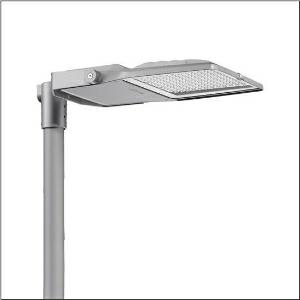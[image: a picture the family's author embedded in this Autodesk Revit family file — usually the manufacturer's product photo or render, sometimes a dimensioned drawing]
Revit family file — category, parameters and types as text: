
# Revit family: floodlight_fl_21_midi___pl33t_5xa7786e2f3a_2de9
name_source: partatom
category: Lighting Fixtures
units: mm (PartAtom-declared; Revit-internal decimal feet)

## family parameters
Cut with Voids When Loaded = No
Host = Face
Light Source = No
Part Type = Normal
Room Calculation Point = No
Round Connector Dimension = Use Diameter
Shared = No

## types (1)
- --- (1 x LED, 26630 lm, 212.4 W, 3000K)
    Apparent Load = 212 VA
    CIE Flux Codes = 26 75 99 100 100
    Color Rendering = 70
    Color Temperature = 3000K
    Default Elevation = 1800 mm
    Description = Floodlight FL 21 midi, floodlight, primary light control with lens, of PMMA, primary optical cover: protective disc, of toughened safety glass, transparent, light distribution: PL33T, light emission: direct distribution, installation type: surface-mounted, LED, High Power LED, rated luminous flux: 26.630lm, luminous efficacy: 125lm/W, light colour: 730, colour temperature: 3000K, control gear: Smart Interface (Zhaga), control: flexible luminous flux parameterisation, time-dependent luminous flux control, constant luminous flux control, overheat protection, pre-setting: logarithmic dimming characteristic, with terminal, 6-pole, mains connection: 220..240V, AC, 50/60Hz, start of lifetime: 212W, end of service life: 231W, reduction: 95W, luminaire housing, of diecast aluminium, powder-coated, SITECO metallic grey (DB 702S), corrosivity category C5 mid according to DIN EN ISO 12944, suitable for swimming pools, chlorine-resistant, sealing non-destructively replaceable, please order mast flange separately, mast bracket, of steel, galvanised, powder-coated, SITECO metallic grey (DB 702S), Smart Interface below and above, protection rating (complete): IP66, insulation class (complete): insulation class II (safety insulation), certification: CE, ENEC, VDE, protection symbol: D, impact resistance: IK08, permissible operating ambient temperature: -40..+40°C, permissible operating ambient temperature for outdoor applications: -40..+50°C, standard: DIN EN 12944, LABS conformity tested according to VDMA 24364:2018-05, packaging unit: 1 piece

Light Distribution: PL33T
    Height = 76 mm
    Lamp = 1 x LED
    Lamp Light Flux = 26630 lm
    Lamp Power = 212.4 W
    Lamp count = 1
    Length = 657 mm
    Luminous efficacy = 125 lm/W
    Manufacturer = Siteco
    ModVariant = No
    Model = 5XA7786E2F3A
    Number of Poles = 1
    OnlyDefault = Yes
    Power Factor = 1
    Product Name = Floodlight FL 21 midi | PL33T
    Product group = floodlight | pylon annexe
    ProductGroupID = 6201
    Protection Class = Protection class II
    Protection Degree = IP 66
    RLX_Detail_Level = 1
    RLX_Emergency_Light_Flux = 0 lm
    RLX_Emergency_Type = 0
    RLX_Emergency_Type_DB = No
    RlxData = <blob elided: 153493 chars, md5=e2bb199f>
    Socket = socket
    Standby Power = 0 W
    System Light Flux = 26630 lm
    System Power = 212 W
    Type Comments = factory setting: luminous flux: 100 % | dim-lin: 254 | 710 mA
    Type Image = l_1007123.jpg
    URL = http://relux.com
    VarID = @adj_150039
    Voltage = 0 V
    Weight = 0.00 kg
    Width = 442 mm

## geometry (parser evidence)
native form markers: Blend x4, Sweep x12
no freeform markers — native parametric forms only
